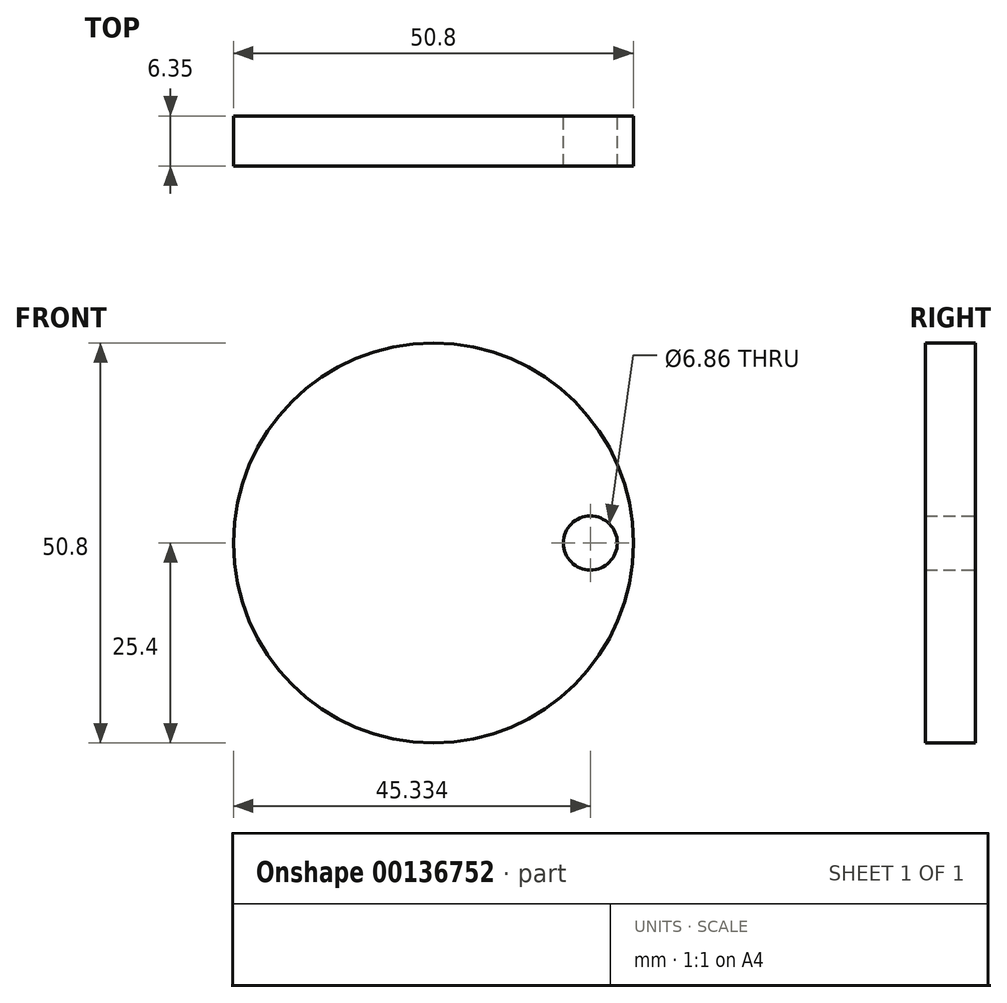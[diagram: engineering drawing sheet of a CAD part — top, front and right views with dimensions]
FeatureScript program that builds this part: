
annotation { "Feature Type Name" : "Feature", "Feature Type Description" : "" }
export const myFeature = defineFeature(function(context is Context, id is Id, definition is map)
    precondition{}
    {
        {
            var Q0;
            Q0=qCreatedBy(makeId("Front.planeOp"),FACE);
            var sketch = newSketch(context, id + "F0", { "sketchPlane" : qUnion([Q0])});
            skCircle(sketch, "E0", {"center": v(0, 0) * mm, "radius": 25.4 * mm});
            skCircle(sketch, "E1", {"center": v(19.93, 0) * mm, "radius": 3.43 * mm});
            skSolve(sketch);
        }
        {
            var Q0;
            Q0=makeQuery(id+"F0.imprint","IMPRINT",FACE,{"disambiguationData":[TD([[makeQuery(id+"F0.imprint","IMPRINT",EDGE,{"derivedFrom":sQuery(id+"F0.wireOp",EDGE,"E0")}),1.0]])]});
            extrude(context, id + "F1", {"entities" : qUnion([Q0]), "depth" : 6.35 * mm});
        }
    });
